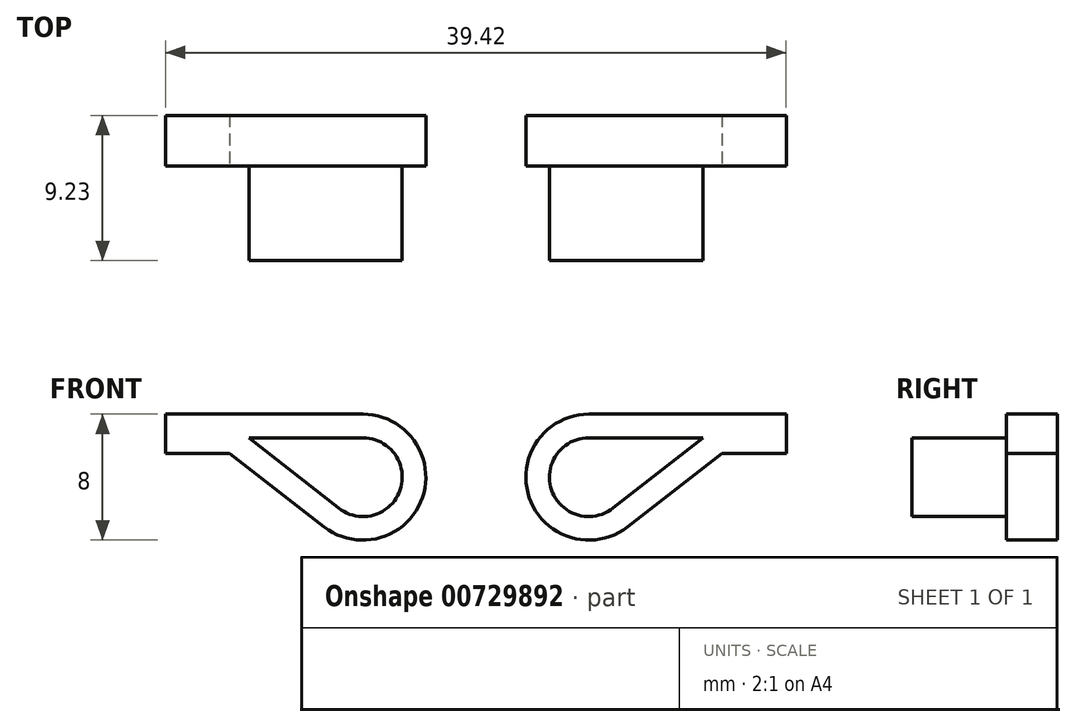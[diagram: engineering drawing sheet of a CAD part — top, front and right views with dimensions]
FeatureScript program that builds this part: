
annotation { "Feature Type Name" : "Feature", "Feature Type Description" : "" }
export const myFeature = defineFeature(function(context is Context, id is Id, definition is map)
    precondition{}
    {
        {
            var Q0;
            Q0=qCreatedBy(makeId("Front.planeOp"),FACE);
            var sketch = newSketch(context, id + "F0", { "sketchPlane" : qUnion([Q0])});
            skLineSegment(sketch, "E0", {"start": v(0, 57.44) * mm, "end": v(0, -47.62) * mm, "construction": true});
            skLineSegment(sketch, "E1.bottom", {"start": v(-60.1, 6.3) * mm, "end": v(60.1, 6.3) * mm});
            skLineSegment(sketch, "E1.top", {"start": v(-60.1, 4.8) * mm, "end": v(60.1, 4.8) * mm});
            skLineSegment(sketch, "E1.left", {"start": v(-60.1, 6.3) * mm, "end": v(-60.1, 4.8) * mm});
            skLineSegment(sketch, "E1.right", {"start": v(60.1, 6.3) * mm, "end": v(60.1, 4.8) * mm});
            skLineSegment(sketch, "E2", {"start": v(-40.92, 0) * mm, "end": v(43.39, 0) * mm, "construction": true});
            skLineSegment(sketch, "E3.MirrorCS", {"start": v(-60.1, -6.3) * mm, "end": v(-60.1, -4.8) * mm});
            skLineSegment(sketch, "E4.MirrorCS", {"start": v(60.1, -6.3) * mm, "end": v(60.1, -4.8) * mm});
            skLineSegment(sketch, "E5.MirrorCS", {"start": v(-60.1, -4.8) * mm, "end": v(60.1, -4.8) * mm});
            skLineSegment(sketch, "E6.MirrorCS", {"start": v(-60.1, -6.3) * mm, "end": v(60.1, -6.3) * mm});
            skSolve(sketch);
        }
        {
            var Q0;
            Q0=qCreatedBy(makeId("Front.planeOp"),FACE);
            var sketch = newSketch(context, id + "F1", { "sketchPlane" : qUnion([Q0])});
            skLineSegment(sketch, "E7.bottom", {"start": v(-20, -2.26) * mm, "end": v(0, -2.26) * mm});
            skLineSegment(sketch, "E7.top", {"start": v(-20, -15.34) * mm, "end": v(0, -15.34) * mm});
            skLineSegment(sketch, "E7.left", {"start": v(-20, -2.26) * mm, "end": v(-20, -4.8) * mm});
            skArc(sketch, "E8", {"start": v(-8.72, -10.77) * mm, "mid": v(-4.81, -9.62) * mm, "end": v(-7.18, -6.3) * mm});
            skArc(sketch, "E9", {"start": v(-9.63, -11.96) * mm, "mid": v(-3.4, -10.1) * mm, "end": v(-7.18, -4.8) * mm});
            skLineSegment(sketch, "E10.0", {"start": v(-60.1, -4.8) * mm, "end": v(60.1, -4.8) * mm, "construction": true});
            skLineSegment(sketch, "E11", {"start": v(-3.18, -8.8) * mm, "end": v(-7.18, -8.8) * mm, "construction": true});
            skLineSegment(sketch, "E12", {"start": v(-20, -7.3) * mm, "end": v(-15.63, -7.3) * mm});
            skLineSegment(sketch, "E13", {"start": v(-15.63, -7.3) * mm, "end": v(-9.63, -11.96) * mm});
            skLineSegment(sketch, "E14", {"start": v(-14.42, -6.3) * mm, "end": v(-8.72, -10.77) * mm});
            skLineSegment(sketch, "E15", {"start": v(-20, -4.8) * mm, "end": v(-7.18, -4.8) * mm});
            skLineSegment(sketch, "E16.trimOffspring", {"start": v(-14.42, -6.3) * mm, "end": v(-7.18, -6.3) * mm, "construction": true});
            skLineSegment(sketch, "E17.trimOffspring", {"start": v(-14.42, -6.3) * mm, "end": v(-7.18, -6.3) * mm});
            skPoint(sketch, "E18.0.start.orphan", {"position": v(-60.1, -6.3) * mm});
            skLineSegment(sketch, "E19.trimOffspring", {"start": v(-20, -7.3) * mm, "end": v(-20, -15.34) * mm});
            skPoint(sketch, "E20.orphan", {"position": v(20, -15.34) * mm});
            skPoint(sketch, "E7.right.start.orphan", {"position": v(20, -2.26) * mm});
            skLineSegment(sketch, "E21", {"start": v(0, 15.66) * mm, "end": v(0, -19.42) * mm, "construction": true});
            skLineSegment(sketch, "E22.MirrorCS", {"start": v(14.42, -6.3) * mm, "end": v(7.18, -6.3) * mm});
            skLineSegment(sketch, "E23.MirrorCS", {"start": v(20, -4.8) * mm, "end": v(7.18, -4.8) * mm});
            skLineSegment(sketch, "E24.MirrorCS", {"start": v(14.42, -6.3) * mm, "end": v(7.18, -6.3) * mm, "construction": true});
            skLineSegment(sketch, "E25.MirrorCS", {"start": v(14.42, -6.3) * mm, "end": v(8.72, -10.77) * mm});
            skLineSegment(sketch, "E26.MirrorCS", {"start": v(15.63, -7.3) * mm, "end": v(9.63, -11.96) * mm});
            skLineSegment(sketch, "E27.MirrorCS", {"start": v(20, -7.3) * mm, "end": v(15.63, -7.3) * mm});
            skLineSegment(sketch, "E28.MirrorCS", {"start": v(3.18, -8.8) * mm, "end": v(7.18, -8.8) * mm, "construction": true});
            skLineSegment(sketch, "E29.MirrorCS", {"start": v(60.1, -4.8) * mm, "end": v(-60.1, -4.8) * mm, "construction": true});
            skArc(sketch, "E30.MirrorCS", {"start": v(9.63, -11.96) * mm, "mid": v(3.4, -10.1) * mm, "end": v(7.18, -4.8) * mm});
            skArc(sketch, "E31.MirrorCS", {"start": v(8.72, -10.77) * mm, "mid": v(4.81, -9.62) * mm, "end": v(7.18, -6.3) * mm});
            skLineSegment(sketch, "E32.MirrorCS", {"start": v(20, -2.26) * mm, "end": v(20, -4.8) * mm});
            skLineSegment(sketch, "E33.MirrorCS", {"start": v(20, -15.34) * mm, "end": v(0, -15.34) * mm});
            skLineSegment(sketch, "E34.MirrorCS", {"start": v(20, -2.26) * mm, "end": v(0, -2.26) * mm});
            skLineSegment(sketch, "E35.MirrorCS", {"start": v(20, -7.3) * mm, "end": v(20, -15.34) * mm});
            skSolve(sketch);
        }
        {
            var Q0;
            Q0 = qSketchRegion(id + "F1", true);
            extrude(context, id + "F2", {"entities" : qUnion([Q0]), "depth" : 8 * mm, "offsetDistance" : 25.4 * mm});
        }
        {
            var Q0;
            Q0=makeQuery(id+"F2.opExtrude","CAP_FACE",FACE,{"disambiguationData":[OSD([sQuery(id+"F1.wireOp",EDGE,"E7.bottom"),sQuery(id+"F1.wireOp",EDGE,"E7.top"),sQuery(id+"F1.wireOp",EDGE,"E7.left"),sQuery(id+"F1.wireOp",EDGE,"E9"),sQuery(id+"F1.wireOp",EDGE,"E12"),sQuery(id+"F1.wireOp",EDGE,"E13"),sQuery(id+"F1.wireOp",EDGE,"E15"),sQuery(id+"F1.wireOp",EDGE,"E19.trimOffspring"),sQuery(id+"F1.wireOp",EDGE,"E23.MirrorCS"),sQuery(id+"F1.wireOp",EDGE,"E26.MirrorCS"),sQuery(id+"F1.wireOp",EDGE,"E27.MirrorCS"),sQuery(id+"F1.wireOp",EDGE,"E30.MirrorCS"),sQuery(id+"F1.wireOp",EDGE,"E32.MirrorCS"),sQuery(id+"F1.wireOp",EDGE,"E33.MirrorCS"),sQuery(id+"F1.wireOp",EDGE,"E34.MirrorCS"),sQuery(id+"F1.wireOp",EDGE,"E35.MirrorCS")])],"isStart":true});
            var sketch = newSketch(context, id + "F3", { "sketchPlane" : qUnion([Q0])});
            skLineSegment(sketch, "E36.bottom", {"start": v(20, -15.34) * mm, "end": v(-20, -15.34) * mm});
            skLineSegment(sketch, "E36.top", {"start": v(20, -2.26) * mm, "end": v(-20, -2.26) * mm});
            skLineSegment(sketch, "E36.left", {"start": v(20, -15.34) * mm, "end": v(20, -2.26) * mm});
            skLineSegment(sketch, "E36.right", {"start": v(-20, -15.34) * mm, "end": v(-20, -2.26) * mm});
            skSolve(sketch);
        }
        {
            var Q0;
            Q0 = qSketchRegion(id + "F3", true);
            extrude(context, id + "F4", {"entities" : qUnion([Q0]), "depth" : -2 * mm, "offsetDistance" : 25.4 * mm});
        }
        {
            var Q0;
            Q0=makeQuery(id+"F4.opExtrude","SWEPT_BODY",BODY,{"disambiguationData":[OSD([sQuery(id+"F3.wireOp",EDGE,"E36.bottom"),sQuery(id+"F3.wireOp",EDGE,"E36.top"),sQuery(id+"F3.wireOp",EDGE,"E36.left"),sQuery(id+"F3.wireOp",EDGE,"E36.right")])]});
            var Q1;
            Q1=makeQuery(id+"F2.opExtrude","SWEPT_BODY",BODY,{"disambiguationData":[OSD([sQuery(id+"F1.wireOp",EDGE,"E7.bottom"),sQuery(id+"F1.wireOp",EDGE,"E7.top"),sQuery(id+"F1.wireOp",EDGE,"E7.left"),sQuery(id+"F1.wireOp",EDGE,"E9"),sQuery(id+"F1.wireOp",EDGE,"E12"),sQuery(id+"F1.wireOp",EDGE,"E13"),sQuery(id+"F1.wireOp",EDGE,"E15"),sQuery(id+"F1.wireOp",EDGE,"E19.trimOffspring"),sQuery(id+"F1.wireOp",EDGE,"E23.MirrorCS"),sQuery(id+"F1.wireOp",EDGE,"E26.MirrorCS"),sQuery(id+"F1.wireOp",EDGE,"E27.MirrorCS"),sQuery(id+"F1.wireOp",EDGE,"E30.MirrorCS"),sQuery(id+"F1.wireOp",EDGE,"E32.MirrorCS"),sQuery(id+"F1.wireOp",EDGE,"E33.MirrorCS"),sQuery(id+"F1.wireOp",EDGE,"E34.MirrorCS"),sQuery(id+"F1.wireOp",EDGE,"E35.MirrorCS")])]});
            booleanBodies(context, id + "F5", {"operationType" : BooleanOperationType.UNION, "tools" : qUnion([Q0, Q1])});
        }
        {
            var Q0;
            Q0=makeQuery(id+"F2.opExtrude","SWEPT_BODY",BODY,{"disambiguationData":[OSD([sQuery(id+"F1.wireOp",EDGE,"E22.MirrorCS"),sQuery(id+"F1.wireOp",EDGE,"E25.MirrorCS"),sQuery(id+"F1.wireOp",EDGE,"E31.MirrorCS")])]});
            var Q1;
            Q1=makeQuery(id+"F4.opExtrude","SWEPT_BODY",BODY,{"disambiguationData":[OSD([sQuery(id+"F3.wireOp",EDGE,"E36.bottom"),sQuery(id+"F3.wireOp",EDGE,"E36.top"),sQuery(id+"F3.wireOp",EDGE,"E36.left"),sQuery(id+"F3.wireOp",EDGE,"E36.right")])]});
            var Q2;
            Q2=makeQuery(id+"F2.opExtrude","SWEPT_BODY",BODY,{"disambiguationData":[OSD([sQuery(id+"F1.wireOp",EDGE,"E8"),sQuery(id+"F1.wireOp",EDGE,"E14"),sQuery(id+"F1.wireOp",EDGE,"E17.trimOffspring")])]});
            booleanBodies(context, id + "F6", {"operationType" : BooleanOperationType.UNION, "tools" : qUnion([Q0, Q1, Q2])});
        }
        {
            var Q0;
            Q0=makeQuery(id+"F2.opExtrude","CAP_FACE",FACE,{"disambiguationData":[OSD([sQuery(id+"F1.wireOp",EDGE,"E7.bottom"),sQuery(id+"F1.wireOp",EDGE,"E7.top"),sQuery(id+"F1.wireOp",EDGE,"E7.left"),sQuery(id+"F1.wireOp",EDGE,"E9"),sQuery(id+"F1.wireOp",EDGE,"E12"),sQuery(id+"F1.wireOp",EDGE,"E13"),sQuery(id+"F1.wireOp",EDGE,"E15"),sQuery(id+"F1.wireOp",EDGE,"E19.trimOffspring"),sQuery(id+"F1.wireOp",EDGE,"E23.MirrorCS"),sQuery(id+"F1.wireOp",EDGE,"E26.MirrorCS"),sQuery(id+"F1.wireOp",EDGE,"E27.MirrorCS"),sQuery(id+"F1.wireOp",EDGE,"E30.MirrorCS"),sQuery(id+"F1.wireOp",EDGE,"E32.MirrorCS"),sQuery(id+"F1.wireOp",EDGE,"E33.MirrorCS"),sQuery(id+"F1.wireOp",EDGE,"E34.MirrorCS"),sQuery(id+"F1.wireOp",EDGE,"E35.MirrorCS")])],"isStart":false});
            var sketch = newSketch(context, id + "F7", { "sketchPlane" : qUnion([Q0])});
            skLineSegment(sketch, "E37.0", {"start": v(20, -7.3) * mm, "end": v(19.71, -7.3) * mm});
            skArc(sketch, "E38", {"start": v(7.18, -15.34) * mm, "mid": v(9.63, -14.86) * mm, "end": v(11.73, -13.5) * mm});
            skLineSegment(sketch, "E39", {"start": v(11.73, -13.5) * mm, "end": v(19.71, -7.3) * mm});
            skPoint(sketch, "E40.0.end.orphan", {"position": v(7.18, -4.8) * mm});
            skPoint(sketch, "E40.0.start.orphan", {"position": v(9.63, -11.96) * mm});
            skLineSegment(sketch, "E41", {"start": v(7.18, -15.34) * mm, "end": v(7.18, -19.2) * mm});
            skLineSegment(sketch, "E42", {"start": v(7.18, -19.2) * mm, "end": v(22.5, -19.2) * mm});
            skLineSegment(sketch, "E43", {"start": v(22.5, -19.2) * mm, "end": v(22.5, -7.3) * mm});
            skLineSegment(sketch, "E44", {"start": v(20, -7.3) * mm, "end": v(22.5, -7.3) * mm});
            skPoint(sketch, "E45.0.start.orphan", {"position": v(15.63, -7.3) * mm});
            skLineSegment(sketch, "E46.MirrorCS", {"start": v(-20, -7.3) * mm, "end": v(-19.71, -7.3) * mm});
            skLineSegment(sketch, "E47.MirrorCS", {"start": v(-20, -7.3) * mm, "end": v(-22.5, -7.3) * mm});
            skLineSegment(sketch, "E48.MirrorCS", {"start": v(-11.73, -13.5) * mm, "end": v(-19.71, -7.3) * mm});
            skArc(sketch, "E49.MirrorCS", {"start": v(-7.18, -15.34) * mm, "mid": v(-9.63, -14.86) * mm, "end": v(-11.73, -13.5) * mm});
            skPoint(sketch, "E50.MirrorP", {"position": v(-7.18, -4.8) * mm});
            skLineSegment(sketch, "E51.MirrorCS", {"start": v(-7.18, -19.2) * mm, "end": v(-22.5, -19.2) * mm});
            skPoint(sketch, "E52.MirrorP", {"position": v(-9.63, -11.96) * mm});
            skPoint(sketch, "E53.MirrorP", {"position": v(-15.63, -7.3) * mm});
            skLineSegment(sketch, "E54.MirrorCS", {"start": v(-7.18, -15.34) * mm, "end": v(-7.18, -19.2) * mm});
            skLineSegment(sketch, "E55.MirrorCS", {"start": v(-22.5, -19.2) * mm, "end": v(-22.5, -7.3) * mm});
            skSolve(sketch);
        }
        {
            var Q0;
            Q0 = qSketchRegion(id + "F7", true);
            extrude(context, id + "F8", {"entities" : qUnion([Q0]), "operationType" : NewBodyOperationType.REMOVE, "oppositeDirection" : true, "depth" : 25.4 * mm, "offsetDistance" : 25.4 * mm});
        }
        {
            var Q0;
            Q0=makeQuery(id+"F5.opBoolean","MERGE",FACE,{"derivedFrom":[makeQuery(id+"F2.opExtrude","SWEPT_FACE",FACE,{"disambiguationData":[OSD([sQuery(id+"F1.wireOp",EDGE,"E32.MirrorCS")])]}),makeQuery(id+"F2.opExtrude","SWEPT_FACE",FACE,{"disambiguationData":[OSD([sQuery(id+"F1.wireOp",EDGE,"E35.MirrorCS")])]}),makeQuery(id+"F4.opExtrude","SWEPT_FACE",FACE,{"disambiguationData":[OSD([sQuery(id+"F3.wireOp",EDGE,"E36.right")])]})]});
            var Q1;
            Q1=makeQuery(id+"F8.boolean.opBoolean","INTERSECT",VERTEX,{"derivedFrom":[makeQuery(id+"F6.opBoolean","MERGE",FACE,{"derivedFrom":[makeQuery(id+"F2.opExtrude","CAP_FACE",FACE,{"disambiguationData":[OSD([sQuery(id+"F1.wireOp",EDGE,"E22.MirrorCS"),sQuery(id+"F1.wireOp",EDGE,"E25.MirrorCS"),sQuery(id+"F1.wireOp",EDGE,"E31.MirrorCS")])],"isStart":true}),makeQuery(id+"F4.opExtrude","CAP_FACE",FACE,{"disambiguationData":[OSD([sQuery(id+"F3.wireOp",EDGE,"E36.bottom"),sQuery(id+"F3.wireOp",EDGE,"E36.top"),sQuery(id+"F3.wireOp",EDGE,"E36.left"),sQuery(id+"F3.wireOp",EDGE,"E36.right")])],"isStart":true})]}),makeQuery(id+"F8.opExtrude","SWEPT_FACE",FACE,{"disambiguationData":[OSD([sQuery(id+"F7.wireOp",EDGE,"E37.0"),sQuery(id+"F7.wireOp",EDGE,"E44")])]}),makeQuery(id+"F8.opExtrude","SWEPT_FACE",FACE,{"disambiguationData":[OSD([sQuery(id+"F7.wireOp",EDGE,"E39")])]})]});
            extrude(context, id + "F9", {"entities" : qUnion([Q0]), "operationType" : NewBodyOperationType.REMOVE, "endBound" : BoundingType.UP_TO_VERTEX, "oppositeDirection" : true, "depth" : 25.4 * mm, "endBoundEntityVertex" : qUnion([Q1]), "offsetDistance" : 25.4 * mm});
        }
        {
            var Q0;
            Q0=makeQuery(id+"F5.opBoolean","MERGE",FACE,{"derivedFrom":[makeQuery(id+"F2.opExtrude","SWEPT_FACE",FACE,{"disambiguationData":[OSD([sQuery(id+"F1.wireOp",EDGE,"E7.left")])]}),makeQuery(id+"F2.opExtrude","SWEPT_FACE",FACE,{"disambiguationData":[OSD([sQuery(id+"F1.wireOp",EDGE,"E19.trimOffspring")])]}),makeQuery(id+"F4.opExtrude","SWEPT_FACE",FACE,{"disambiguationData":[OSD([sQuery(id+"F3.wireOp",EDGE,"E36.left")])]})]});
            var Q1;
            Q1=makeQuery(id+"F8.boolean.opBoolean","INTERSECT",VERTEX,{"derivedFrom":[makeQuery(id+"F6.opBoolean","MERGE",FACE,{"derivedFrom":[makeQuery(id+"F2.opExtrude","CAP_FACE",FACE,{"disambiguationData":[OSD([sQuery(id+"F1.wireOp",EDGE,"E22.MirrorCS"),sQuery(id+"F1.wireOp",EDGE,"E25.MirrorCS"),sQuery(id+"F1.wireOp",EDGE,"E31.MirrorCS")])],"isStart":true}),makeQuery(id+"F4.opExtrude","CAP_FACE",FACE,{"disambiguationData":[OSD([sQuery(id+"F3.wireOp",EDGE,"E36.bottom"),sQuery(id+"F3.wireOp",EDGE,"E36.top"),sQuery(id+"F3.wireOp",EDGE,"E36.left"),sQuery(id+"F3.wireOp",EDGE,"E36.right")])],"isStart":true})]}),makeQuery(id+"F8.opExtrude","SWEPT_FACE",FACE,{"disambiguationData":[OSD([sQuery(id+"F7.wireOp",EDGE,"E46.MirrorCS"),sQuery(id+"F7.wireOp",EDGE,"E47.MirrorCS")])]}),makeQuery(id+"F8.opExtrude","SWEPT_FACE",FACE,{"disambiguationData":[OSD([sQuery(id+"F7.wireOp",EDGE,"E48.MirrorCS")])]})]});
            extrude(context, id + "F10", {"entities" : qUnion([Q0]), "operationType" : NewBodyOperationType.REMOVE, "endBound" : BoundingType.UP_TO_VERTEX, "oppositeDirection" : true, "depth" : 25.4 * mm, "endBoundEntityVertex" : qUnion([Q1]), "offsetDistance" : 25.4 * mm});
        }
        {
            var Q0;
            Q0=makeQuery(id+"F6.opBoolean","MERGE",FACE,{"derivedFrom":[makeQuery(id+"F2.opExtrude","CAP_FACE",FACE,{"disambiguationData":[OSD([sQuery(id+"F1.wireOp",EDGE,"E22.MirrorCS"),sQuery(id+"F1.wireOp",EDGE,"E25.MirrorCS"),sQuery(id+"F1.wireOp",EDGE,"E31.MirrorCS")])],"isStart":true}),makeQuery(id+"F4.opExtrude","CAP_FACE",FACE,{"disambiguationData":[OSD([sQuery(id+"F3.wireOp",EDGE,"E36.bottom"),sQuery(id+"F3.wireOp",EDGE,"E36.top"),sQuery(id+"F3.wireOp",EDGE,"E36.left"),sQuery(id+"F3.wireOp",EDGE,"E36.right")])],"isStart":true})]});
            extrude(context, id + "F11", {"entities" : qUnion([Q0]), "operationType" : NewBodyOperationType.ADD, "depth" : 1.23 * mm, "offsetDistance" : 25.4 * mm});
        }
        {
            var Q0;
            Q0=makeQuery(id+"F2.opExtrude","CAP_FACE",FACE,{"disambiguationData":[OSD([sQuery(id+"F1.wireOp",EDGE,"E7.bottom"),sQuery(id+"F1.wireOp",EDGE,"E7.top"),sQuery(id+"F1.wireOp",EDGE,"E7.left"),sQuery(id+"F1.wireOp",EDGE,"E9"),sQuery(id+"F1.wireOp",EDGE,"E12"),sQuery(id+"F1.wireOp",EDGE,"E13"),sQuery(id+"F1.wireOp",EDGE,"E15"),sQuery(id+"F1.wireOp",EDGE,"E19.trimOffspring"),sQuery(id+"F1.wireOp",EDGE,"E23.MirrorCS"),sQuery(id+"F1.wireOp",EDGE,"E26.MirrorCS"),sQuery(id+"F1.wireOp",EDGE,"E27.MirrorCS"),sQuery(id+"F1.wireOp",EDGE,"E30.MirrorCS"),sQuery(id+"F1.wireOp",EDGE,"E32.MirrorCS"),sQuery(id+"F1.wireOp",EDGE,"E33.MirrorCS"),sQuery(id+"F1.wireOp",EDGE,"E34.MirrorCS"),sQuery(id+"F1.wireOp",EDGE,"E35.MirrorCS")])],"isStart":false});
            var sketch = newSketch(context, id + "F12", { "sketchPlane" : qUnion([Q0])});
            skLineSegment(sketch, "E56", {"start": v(0, -15.34) * mm, "end": v(0, -2.26) * mm, "construction": true});
            skPoint(sketch, "E57", {"position": v(0, -8.8) * mm});
            skLineSegment(sketch, "E58", {"start": v(3.18, -8.8) * mm, "end": v(-3.18, -8.8) * mm, "construction": true});
            skLineSegment(sketch, "E59", {"start": v(0, -11.34) * mm, "end": v(0, -6.26) * mm});
            skArc(sketch, "E60.0.startCap", {"start": v(1.5, -11.34) * mm, "mid": v(0, -12.84) * mm, "end": v(-1.5, -11.34) * mm});
            skArc(sketch, "E60.0.endCap", {"start": v(-1.5, -6.26) * mm, "mid": v(0, -4.76) * mm, "end": v(1.5, -6.26) * mm});
            skLineSegment(sketch, "E60.0.left", {"start": v(-1.5, -11.34) * mm, "end": v(-1.5, -6.26) * mm});
            skLineSegment(sketch, "E60.0.right", {"start": v(1.5, -11.34) * mm, "end": v(1.5, -6.26) * mm});
            skSolve(sketch);
        }
        {
            var Q0;
            Q0=makeQuery(id+"F12.imprint","IMPRINT",FACE,{"disambiguationData":[TD([[makeQuery(id+"F12.imprint","IMPRINT",EDGE,{"derivedFrom":sQuery(id+"F12.wireOp",EDGE,"E60.0.startCap")}),-1.0]])]});
            var Q1;
            Q1 = qSketchRegion(id + "F12", true);
            extrude(context, id + "F13", {"entities" : qUnion([Q0, Q1]), "operationType" : NewBodyOperationType.REMOVE, "oppositeDirection" : true, "depth" : 25.4 * mm, "offsetDistance" : 25.4 * mm});
        }
    });
